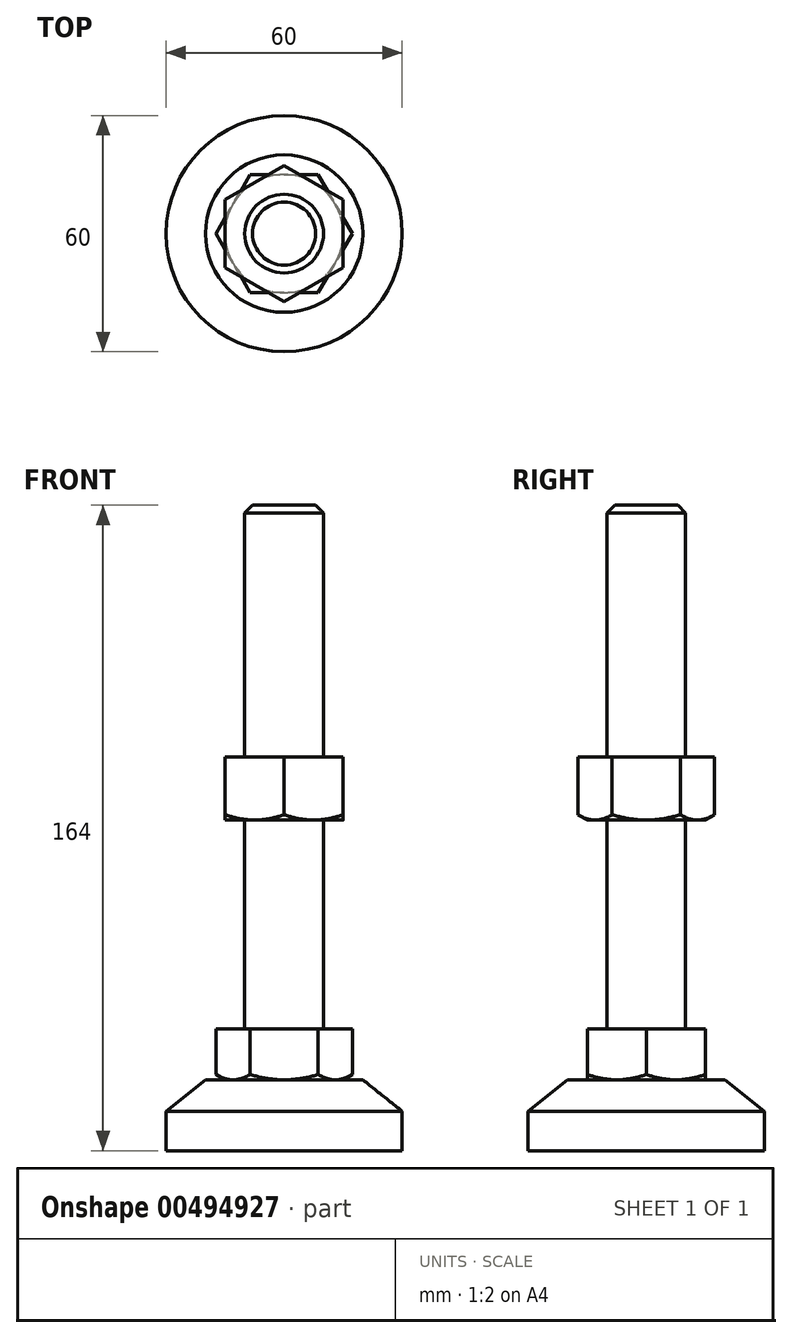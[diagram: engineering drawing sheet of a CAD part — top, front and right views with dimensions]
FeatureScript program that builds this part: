
annotation { "Feature Type Name" : "Feature", "Feature Type Description" : "" }
export const myFeature = defineFeature(function(context is Context, id is Id, definition is map)
    precondition{}
    {
        {
            var Q0;
            Q0=qCreatedBy(makeId("Top.planeOp"),FACE);
            var sketch = newSketch(context, id + "F0", { "sketchPlane" : qUnion([Q0])});
            skCircle(sketch, "E0", {"center": v(0, 0) * mm, "radius": 30 * mm});
            skSolve(sketch);
        }
        {
            var Q0;
            Q0=qSketchRegion(id+"F0",true);
            extrude(context, id + "F1", {"entities" : qUnion([Q0]), "depth" : 18 * mm});
        }
        {
            var Q0;
            Q0=makeQuery(id+"F1.opExtrude","CAP_FACE",FACE,{"disambiguationData":[OSD([sQuery(id+"F0.wireOp",EDGE,"E0")])],"isStart":false});
            var sketch = newSketch(context, id + "F2", { "sketchPlane" : qUnion([Q0])});
            skCircle(sketch, "E1", {"center": v(0, 0) * mm, "radius": 10 * mm});
            skSolve(sketch);
        }
        {
            var Q0;
            Q0=qSketchRegion(id+"F2",true);
            extrude(context, id + "F3", {"entities" : qUnion([Q0]), "operationType" : NewBodyOperationType.ADD, "depth" : 146 * mm});
        }
        {
            var Q0;
            Q0=makeQuery(id+"F3.opExtrude","CAP_EDGE",EDGE,{"disambiguationData":[OSD([sQuery(id+"F2.wireOp",EDGE,"E1")])],"isStart":false});
            chamfer(context, id + "F4", {"entities" : qUnion([Q0]), "width" : 2 * mm, "tangentPropagation" : true});
        }
        {
            var Q0;
            Q0=makeQuery(id+"F1.opExtrude","CAP_EDGE",EDGE,{"disambiguationData":[OSD([sQuery(id+"F0.wireOp",EDGE,"E0")])],"isStart":false});
            chamfer(context, id + "F5", {"entities" : qUnion([Q0]), "chamferType" : ChamferType.TWO_OFFSETS, "width1" : 10 * mm, "oppositeDirection" : false, "width2" : 8 * mm, "tangentPropagation" : true});
        }
        {
            var Q0;
            Q0=makeQuery(id+"F1.opExtrude","CAP_FACE",FACE,{"disambiguationData":[OSD([sQuery(id+"F0.wireOp",EDGE,"E0")])],"isStart":false});
            var sketch = newSketch(context, id + "F6", { "sketchPlane" : qUnion([Q0])});
            skCircle(sketch, "E2.cCircle", {"center": v(0, 0) * mm, "radius": 15 * mm, "construction": true});
            skLineSegment(sketch, "E2.0", {"start": v(17.32, 0) * mm, "end": v(8.66, -15) * mm});
            skLineSegment(sketch, "E2.1", {"start": v(8.66, -15) * mm, "end": v(-8.66, -15) * mm});
            skLineSegment(sketch, "E2.2", {"start": v(-8.66, -15) * mm, "end": v(-17.32, 0) * mm});
            skLineSegment(sketch, "E2.3", {"start": v(-17.32, 0) * mm, "end": v(-8.66, 15) * mm});
            skLineSegment(sketch, "E2.4", {"start": v(-8.66, 15) * mm, "end": v(8.66, 15) * mm});
            skLineSegment(sketch, "E2.5", {"start": v(8.66, 15) * mm, "end": v(17.32, 0) * mm});
            skPoint(sketch, "E2.0.midPoint", {"position": v(13, -7.5) * mm});
            skSolve(sketch);
        }
        {
            var Q0;
            Q0=qSketchRegion(id+"F6",true);
            extrude(context, id + "F7", {"entities" : qUnion([Q0]), "operationType" : NewBodyOperationType.ADD, "depth" : 13 * mm});
        }
        {
            var Q0;
            Q0=qCreatedBy(makeId("Top.planeOp"),FACE);
            cPlane(context, id + "F8", {"entities" : qUnion([Q0]), "cplaneType" : CPlaneType.OFFSET, "offset" : 100 * mm, "width" : 150 * mm, "height" : 150 * mm});
        }
        {
            var Q0;
            Q0=qCreatedBy(id+"F8.planeOp",FACE);
            var sketch = newSketch(context, id + "F9", { "sketchPlane" : qUnion([Q0])});
            skCircle(sketch, "E3.cCircle", {"center": v(0, 0) * mm, "radius": 15 * mm, "construction": true});
            skLineSegment(sketch, "E3.0", {"start": v(0, 17.32) * mm, "end": v(15, 8.66) * mm});
            skLineSegment(sketch, "E3.1", {"start": v(15, 8.66) * mm, "end": v(15, -8.66) * mm});
            skLineSegment(sketch, "E3.2", {"start": v(15, -8.66) * mm, "end": v(0, -17.32) * mm});
            skLineSegment(sketch, "E3.3", {"start": v(0, -17.32) * mm, "end": v(-15, -8.66) * mm});
            skLineSegment(sketch, "E3.4", {"start": v(-15, -8.66) * mm, "end": v(-15, 8.66) * mm});
            skLineSegment(sketch, "E3.5", {"start": v(-15, 8.66) * mm, "end": v(0, 17.32) * mm});
            skPoint(sketch, "E3.0.midPoint", {"position": v(7.5, 13) * mm});
            skSolve(sketch);
        }
        {
            var Q0;
            Q0=qSketchRegion(id+"F9",true);
            extrude(context, id + "F10", {"entities" : qUnion([Q0]), "operationType" : NewBodyOperationType.ADD, "oppositeDirection" : true, "depth" : 16 * mm});
        }
        {
            var Q0;
            Q0=qCreatedBy(makeId("Right.planeOp"),FACE);
            var sketch = newSketch(context, id + "F11", { "sketchPlane" : qUnion([Q0])});
            skLineSegment(sketch, "E4", {"start": v(17.32, 84) * mm, "end": v(17.32, 85.34) * mm});
            skLineSegment(sketch, "E5", {"start": v(17.32, 85.34) * mm, "end": v(15, 84) * mm});
            skLineSegment(sketch, "E6", {"start": v(15, 84) * mm, "end": v(17.32, 84) * mm});
            skSolve(sketch);
        }
        {
            var Q0;
            Q0=qSketchRegion(id+"F11",true);
            var Q1;
            {var subQ0=sQuery(id+"F2.wireOp",EDGE,"E1");Q1=makeQuery(id+"F10.boolean.opBoolean","SPLIT",FACE,{"disambiguationData":[TD([makeQuery(id+"F4.opChamfer","BLEND_FACE",FACE,{"disambiguationData":[OSD([subQ0])]})])],"derivedFrom":makeQuery(id+"F3.opExtrude","SWEPT_FACE",FACE,{"disambiguationData":[OSD([subQ0])]})});}
            revolve(context, id + "F12", {"operationType" : NewBodyOperationType.REMOVE, "entities" : qUnion([Q0]), "axis" : qUnion([Q1]), "revolveType" : RevolveType.FULL, "oppositeDirection" : true});
        }
        {
            var Q0;
            Q0=qCreatedBy(makeId("Front.planeOp"),FACE);
            var sketch = newSketch(context, id + "F13", { "sketchPlane" : qUnion([Q0])});
            skLineSegment(sketch, "E7", {"start": v(-15, 18) * mm, "end": v(-17.32, 18) * mm});
            skLineSegment(sketch, "E8", {"start": v(-17.32, 18) * mm, "end": v(-17.32, 19.34) * mm});
            skLineSegment(sketch, "E9", {"start": v(-17.32, 19.34) * mm, "end": v(-15, 18) * mm});
            skSolve(sketch);
        }
        {
            var Q0;
            Q0=qSketchRegion(id+"F13",true);
            var Q1;
            Q1=makeQuery(id+"F10.boolean.opBoolean","SPLIT",FACE,{"disambiguationData":[TD([makeQuery(id+"F7.opExtrude","CAP_FACE",FACE,{"disambiguationData":[OSD([sQuery(id+"F6.wireOp",EDGE,"E2.0"),sQuery(id+"F6.wireOp",EDGE,"E2.1"),sQuery(id+"F6.wireOp",EDGE,"E2.2"),sQuery(id+"F6.wireOp",EDGE,"E2.3"),sQuery(id+"F6.wireOp",EDGE,"E2.4"),sQuery(id+"F6.wireOp",EDGE,"E2.5")])],"isStart":false})])],"derivedFrom":makeQuery(id+"F3.opExtrude","SWEPT_FACE",FACE,{"disambiguationData":[OSD([sQuery(id+"F2.wireOp",EDGE,"E1")])]})});
            revolve(context, id + "F14", {"operationType" : NewBodyOperationType.REMOVE, "entities" : qUnion([Q0]), "axis" : qUnion([Q1]), "revolveType" : RevolveType.FULL, "oppositeDirection" : true});
        }
    });
